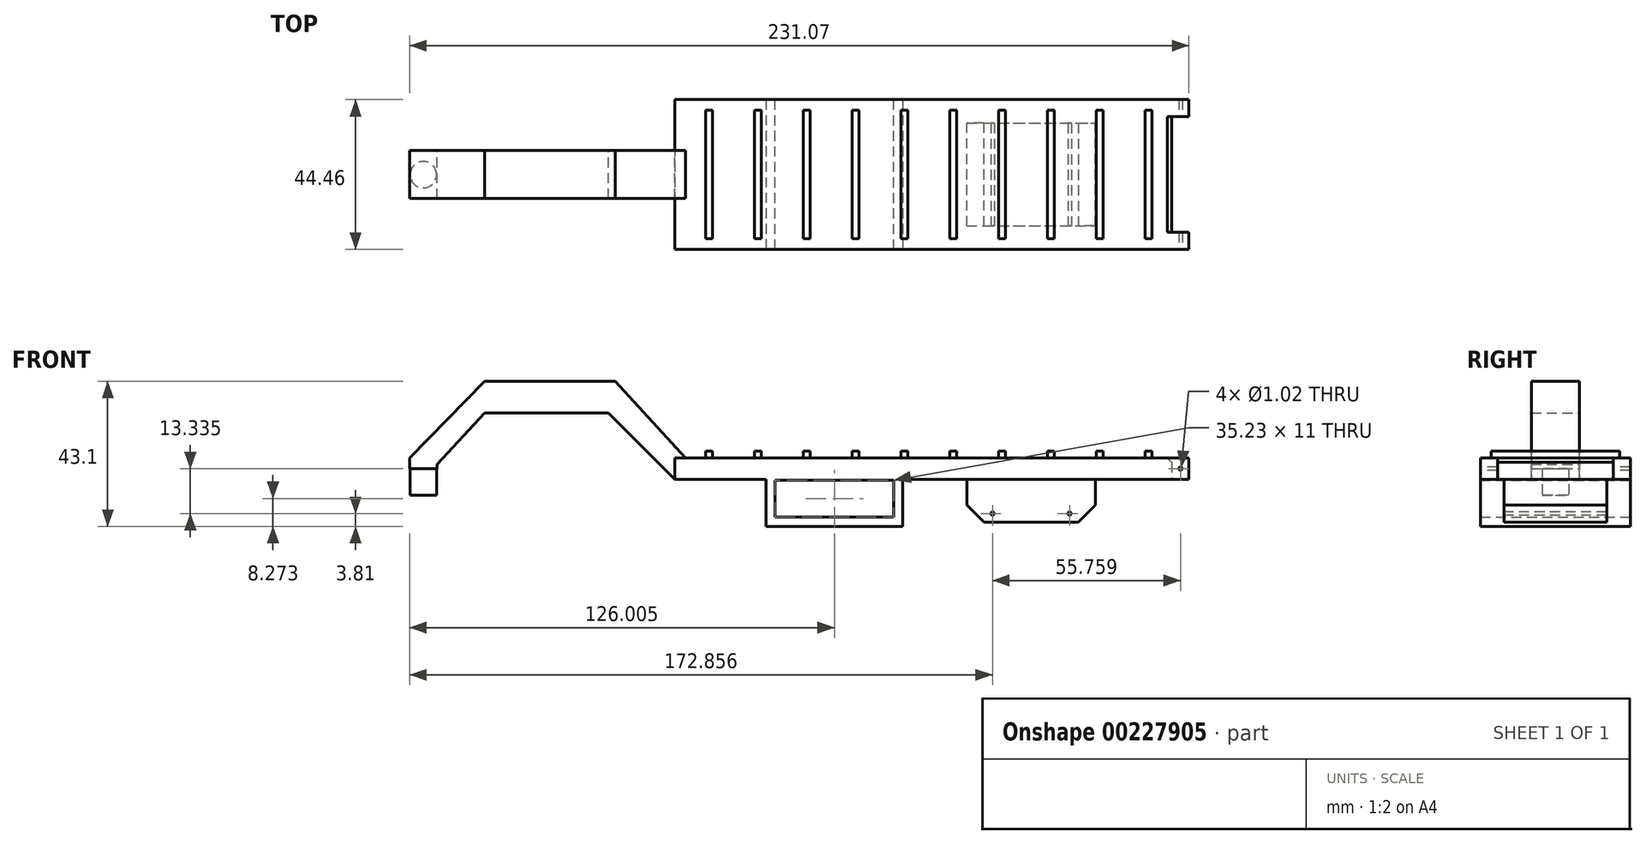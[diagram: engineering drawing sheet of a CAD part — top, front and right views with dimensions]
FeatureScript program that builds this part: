
annotation { "Feature Type Name" : "Feature", "Feature Type Description" : "" }
export const myFeature = defineFeature(function(context is Context, id is Id, definition is map)
    precondition{}
    {
        {
            var Q0;
            Q0=qCreatedBy(makeId("Top.planeOp"),FACE);
            var sketch = newSketch(context, id + "F0", { "sketchPlane" : qUnion([Q0])});
            skLineSegment(sketch, "E0.bottom", {"start": v(-76.2, 22.23) * mm, "end": v(76.2, 22.23) * mm});
            skLineSegment(sketch, "E0.top", {"start": v(-76.2, -22.23) * mm, "end": v(76.2, -22.23) * mm});
            skLineSegment(sketch, "E0.left", {"start": v(-76.2, 22.23) * mm, "end": v(-76.2, -22.23) * mm});
            skLineSegment(sketch, "E0.right", {"start": v(76.2, 22.23) * mm, "end": v(76.2, -22.23) * mm});
            skPoint(sketch, "E0.middle", {"position": v(0, 0) * mm});
            skSolve(sketch);
        }
        {
            var Q0;
            Q0=makeQuery(id+"F0.imprint","IMPRINT",FACE,{"disambiguationData":[TD([[makeQuery(id+"F0.imprint","IMPRINT",EDGE,{"derivedFrom":sQuery(id+"F0.wireOp",EDGE,"E0.bottom")}),-1.0]])]});
            extrude(context, id + "F1", {"entities" : qUnion([Q0]), "oppositeDirection" : true, "depth" : 6.35 * mm});
        }
        {
            var Q0;
            Q0=makeQuery(id+"F1.opExtrude","CAP_FACE",FACE,{"disambiguationData":[OSD([sQuery(id+"F0.wireOp",EDGE,"E0.bottom"),sQuery(id+"F0.wireOp",EDGE,"E0.top"),sQuery(id+"F0.wireOp",EDGE,"E0.left"),sQuery(id+"F0.wireOp",EDGE,"E0.right")])],"isStart":false});
            var sketch = newSketch(context, id + "F2", { "sketchPlane" : qUnion([Q0])});
            skLineSegment(sketch, "E1.bottom", {"start": v(10.37, 15.24) * mm, "end": v(48.47, 15.24) * mm});
            skLineSegment(sketch, "E1.top", {"start": v(10.37, -15.24) * mm, "end": v(48.47, -15.24) * mm});
            skLineSegment(sketch, "E1.left", {"start": v(10.37, 15.24) * mm, "end": v(10.37, -15.24) * mm});
            skLineSegment(sketch, "E1.right", {"start": v(48.47, 15.24) * mm, "end": v(48.47, -15.24) * mm});
            skPoint(sketch, "E1.middle", {"position": v(29.42, 0) * mm});
            skLineSegment(sketch, "E2.bottom", {"start": v(76.2, 17.14) * mm, "end": v(71.12, 17.14) * mm});
            skLineSegment(sketch, "E2.top", {"start": v(76.2, -17.14) * mm, "end": v(71.12, -17.14) * mm});
            skLineSegment(sketch, "E2.left", {"start": v(76.2, 17.14) * mm, "end": v(76.2, -17.14) * mm});
            skLineSegment(sketch, "E2.right", {"start": v(71.12, 17.14) * mm, "end": v(71.12, -17.14) * mm});
            skSolve(sketch);
        }
        {
            var Q0;
            Q0=makeQuery(id+"F2.imprint","IMPRINT",FACE,{"disambiguationData":[TD([[makeQuery(id+"F2.imprint","IMPRINT",EDGE,{"derivedFrom":sQuery(id+"F2.wireOp",EDGE,"E1.bottom")}),-1.0]])]});
            extrude(context, id + "F3", {"entities" : qUnion([Q0]), "operationType" : NewBodyOperationType.ADD, "depth" : 12.7 * mm});
        }
        {
            var Q0;
            Q0=makeQuery(id+"F2.imprint","IMPRINT",FACE,{"disambiguationData":[TD([[makeQuery(id+"F2.imprint","IMPRINT",EDGE,{"derivedFrom":sQuery(id+"F2.wireOp",EDGE,"E2.bottom")}),1.0]])]});
            extrude(context, id + "F4", {"entities" : qUnion([Q0]), "operationType" : NewBodyOperationType.REMOVE, "oppositeDirection" : true, "depth" : 25.4 * mm});
        }
        {
            var Q0;
            Q0=makeQuery(id+"F1.opExtrude","SWEPT_FACE",FACE,{"disambiguationData":[OSD([sQuery(id+"F0.wireOp",EDGE,"E0.top")])]});
            var sketch = newSketch(context, id + "F5", { "sketchPlane" : qUnion([Q0])});
            skCircle(sketch, "E3", {"center": v(73.74, -3.18) * mm, "radius": 0.5 * mm});
            skPoint(sketch, "E3.centerSnap0", {"position": v(76.2, -3.18) * mm});
            skSolve(sketch);
        }
        {
            var Q0;
            Q0=makeQuery(id+"F5.imprint","IMPRINT",FACE,{"disambiguationData":[TD([[makeQuery(id+"F5.imprint","IMPRINT",EDGE,{"derivedFrom":sQuery(id+"F5.wireOp",EDGE,"E3")}),1.0]])]});
            extrude(context, id + "F6", {"entities" : qUnion([Q0]), "operationType" : NewBodyOperationType.REMOVE, "oppositeDirection" : true, "depth" : 49.23 * mm});
        }
        {
            var Q0;
            Q0=makeQuery(id+"F3.opExtrude","CAP_EDGE",EDGE,{"disambiguationData":[OSD([sQuery(id+"F2.wireOp",EDGE,"E1.left")])],"isStart":false});
            var Q1;
            Q1=makeQuery(id+"F3.opExtrude","CAP_EDGE",EDGE,{"disambiguationData":[OSD([sQuery(id+"F2.wireOp",EDGE,"E1.right")])],"isStart":false});
            chamfer(context, id + "F7", {"entities" : qUnion([Q0, Q1]), "width" : 5.08 * mm, "tangentPropagation" : true});
        }
        {
            var Q0;
            Q0=makeQuery(id+"F4.boolean.opBoolean","INTERSECT",EDGE,{"derivedFrom":[makeQuery(id+"F1.opExtrude","CAP_FACE",FACE,{"disambiguationData":[OSD([sQuery(id+"F0.wireOp",EDGE,"E0.bottom"),sQuery(id+"F0.wireOp",EDGE,"E0.top"),sQuery(id+"F0.wireOp",EDGE,"E0.left"),sQuery(id+"F0.wireOp",EDGE,"E0.right")])],"isStart":true}),makeQuery(id+"F4.opExtrude","SWEPT_FACE",FACE,{"disambiguationData":[OSD([sQuery(id+"F2.wireOp",EDGE,"E2.right")])]})]});
            var Q1;
            Q1=makeQuery(id+"F4.boolean.opBoolean","COPY",EDGE,{"derivedFrom":makeQuery(id+"F4.opExtrude","CAP_EDGE",EDGE,{"disambiguationData":[OSD([sQuery(id+"F2.wireOp",EDGE,"E2.right")])],"isStart":true})});
            chamfer(context, id + "F8", {"entities" : qUnion([Q0, Q1]), "width" : 1.27 * mm, "tangentPropagation" : true});
        }
        {
            var Q0;
            Q0=qCreatedBy(makeId("Front.planeOp"),FACE);
            var sketch = newSketch(context, id + "F9", { "sketchPlane" : qUnion([Q0])});
            skLineSegment(sketch, "E4", {"start": v(-73, 0) * mm, "end": v(-93.79, 22.78) * mm});
            skLineSegment(sketch, "E5", {"start": v(-93.79, 22.78) * mm, "end": v(-132.6, 22.78) * mm});
            skLineSegment(sketch, "E6", {"start": v(-132.6, 22.78) * mm, "end": v(-154.87, 0) * mm});
            skLineSegment(sketch, "E7", {"start": v(-154.87, 0) * mm, "end": v(-154.87, -11.08) * mm});
            skLineSegment(sketch, "E8", {"start": v(-154.87, -11.08) * mm, "end": v(-146.63, -11.08) * mm});
            skLineSegment(sketch, "E9", {"start": v(-146.63, -11.08) * mm, "end": v(-146.63, -1.92) * mm});
            skLineSegment(sketch, "E10", {"start": v(-146.63, -1.92) * mm, "end": v(-132.6, 13.28) * mm});
            skLineSegment(sketch, "E11", {"start": v(-132.6, 13.28) * mm, "end": v(-95.88, 13.28) * mm});
            skLineSegment(sketch, "E12", {"start": v(-95.88, 13.28) * mm, "end": v(-76.2, -6.3) * mm});
            skLineSegment(sketch, "E13", {"start": v(-76.2, -6.3) * mm, "end": v(-76.2, 0) * mm});
            skLineSegment(sketch, "E14", {"start": v(-76.2, 0) * mm, "end": v(-73, 0) * mm});
            skSolve(sketch);
        }
        {
            var Q0;
            Q0=makeQuery(id+"F9.imprint","IMPRINT",FACE,{"disambiguationData":[TD([[makeQuery(id+"F9.imprint","IMPRINT",EDGE,{"derivedFrom":sQuery(id+"F9.wireOp",EDGE,"E4")}),1.0]])]});
            extrude(context, id + "F10", {"entities" : qUnion([Q0]), "operationType" : NewBodyOperationType.ADD, "endBound" : BoundingType.SYMMETRIC, "depth" : 14.22 * mm});
        }
        {
            var Q0;
            Q0=makeQuery(id+"F10.opExtrude","SWEPT_FACE",FACE,{"disambiguationData":[OSD([sQuery(id+"F9.wireOp",EDGE,"E8")])]});
            var sketch = newSketch(context, id + "F11", { "sketchPlane" : qUnion([Q0])});
            skCircle(sketch, "E15", {"center": v(-150.75, 0) * mm, "radius": 3.92 * mm});
            skPoint(sketch, "E15.centerSnap0", {"position": v(-150.75, 7.11) * mm});
            skLineSegment(sketch, "E16.bottom", {"start": v(-154.87, 7.11) * mm, "end": v(-146.63, 7.11) * mm});
            skLineSegment(sketch, "E16.top", {"start": v(-154.87, -7.11) * mm, "end": v(-146.63, -7.11) * mm});
            skLineSegment(sketch, "E16.left", {"start": v(-154.87, 7.11) * mm, "end": v(-154.87, -7.11) * mm});
            skLineSegment(sketch, "E16.right", {"start": v(-146.63, 7.11) * mm, "end": v(-146.63, -7.11) * mm});
            skSolve(sketch);
        }
        {
            var Q0;
            Q0=makeQuery(id+"F11.imprint","IMPRINT",FACE,{"disambiguationData":[TD([[makeQuery(id+"F11.imprint","IMPRINT",EDGE,{"derivedFrom":sQuery(id+"F11.wireOp",EDGE,"E15")}),-1.0]])]});
            extrude(context, id + "F12", {"entities" : qUnion([Q0]), "operationType" : NewBodyOperationType.REMOVE, "oppositeDirection" : true, "depth" : 7.87 * mm});
        }
        {
            var Q0;
            Q0=makeQuery(id+"F1.opExtrude","CAP_FACE",FACE,{"disambiguationData":[OSD([sQuery(id+"F0.wireOp",EDGE,"E0.bottom"),sQuery(id+"F0.wireOp",EDGE,"E0.top"),sQuery(id+"F0.wireOp",EDGE,"E0.left"),sQuery(id+"F0.wireOp",EDGE,"E0.right")])],"isStart":true});
            var sketch = newSketch(context, id + "F13", { "sketchPlane" : qUnion([Q0])});
            skLineSegment(sketch, "E17.bottom", {"start": v(-67, 19.05) * mm, "end": v(-64.96, 19.05) * mm});
            skLineSegment(sketch, "E17.top", {"start": v(-67, -19.05) * mm, "end": v(-64.96, -19.05) * mm});
            skLineSegment(sketch, "E17.left", {"start": v(-67, 19.05) * mm, "end": v(-67, -19.05) * mm});
            skLineSegment(sketch, "E17.right", {"start": v(-64.96, 19.05) * mm, "end": v(-64.96, -19.05) * mm});
            skPoint(sketch, "E17.middle", {"position": v(-65.98, 0) * mm});
            skLineSegment(sketch, "E18.1.0.0", {"start": v(-52.52, 19.05) * mm, "end": v(-50.48, 19.05) * mm});
            skLineSegment(sketch, "E18.1.0.1", {"start": v(-52.52, 19.05) * mm, "end": v(-52.52, -19.05) * mm});
            skLineSegment(sketch, "E18.1.0.2", {"start": v(-52.52, -19.05) * mm, "end": v(-50.48, -19.05) * mm});
            skLineSegment(sketch, "E18.1.0.3", {"start": v(-50.48, 19.05) * mm, "end": v(-50.48, -19.05) * mm});
            skLineSegment(sketch, "E18.2.0.0", {"start": v(-38.04, 19.05) * mm, "end": v(-36, 19.05) * mm});
            skLineSegment(sketch, "E18.2.0.1", {"start": v(-38.04, 19.05) * mm, "end": v(-38.04, -19.05) * mm});
            skLineSegment(sketch, "E18.2.0.2", {"start": v(-38.04, -19.05) * mm, "end": v(-36, -19.05) * mm});
            skLineSegment(sketch, "E18.2.0.3", {"start": v(-36, 19.05) * mm, "end": v(-36, -19.05) * mm});
            skLineSegment(sketch, "E18.3.0.0", {"start": v(-23.56, 19.05) * mm, "end": v(-21.53, 19.05) * mm});
            skLineSegment(sketch, "E18.3.0.1", {"start": v(-23.56, 19.05) * mm, "end": v(-23.56, -19.05) * mm});
            skLineSegment(sketch, "E18.3.0.2", {"start": v(-23.56, -19.05) * mm, "end": v(-21.53, -19.05) * mm});
            skLineSegment(sketch, "E18.3.0.3", {"start": v(-21.53, 19.05) * mm, "end": v(-21.53, -19.05) * mm});
            skLineSegment(sketch, "E18.4.0.0", {"start": v(-9.08, 19.05) * mm, "end": v(-7.05, 19.05) * mm});
            skLineSegment(sketch, "E18.4.0.1", {"start": v(-9.08, 19.05) * mm, "end": v(-9.08, -19.05) * mm});
            skLineSegment(sketch, "E18.4.0.2", {"start": v(-9.08, -19.05) * mm, "end": v(-7.05, -19.05) * mm});
            skLineSegment(sketch, "E18.4.0.3", {"start": v(-7.05, 19.05) * mm, "end": v(-7.05, -19.05) * mm});
            skLineSegment(sketch, "E18.5.0.0", {"start": v(5.4, 19.05) * mm, "end": v(7.43, 19.05) * mm});
            skLineSegment(sketch, "E18.5.0.1", {"start": v(5.4, 19.05) * mm, "end": v(5.4, -19.05) * mm});
            skLineSegment(sketch, "E18.5.0.2", {"start": v(5.4, -19.05) * mm, "end": v(7.43, -19.05) * mm});
            skLineSegment(sketch, "E18.5.0.3", {"start": v(7.43, 19.05) * mm, "end": v(7.43, -19.05) * mm});
            skLineSegment(sketch, "E18.6.0.0", {"start": v(19.87, 19.05) * mm, "end": v(21.9, 19.05) * mm});
            skLineSegment(sketch, "E18.6.0.1", {"start": v(19.87, 19.05) * mm, "end": v(19.87, -19.05) * mm});
            skLineSegment(sketch, "E18.6.0.2", {"start": v(19.87, -19.05) * mm, "end": v(21.9, -19.05) * mm});
            skLineSegment(sketch, "E18.6.0.3", {"start": v(21.9, 19.05) * mm, "end": v(21.9, -19.05) * mm});
            skLineSegment(sketch, "E18.7.0.0", {"start": v(34.35, 19.05) * mm, "end": v(36.38, 19.05) * mm});
            skLineSegment(sketch, "E18.7.0.1", {"start": v(34.35, 19.05) * mm, "end": v(34.35, -19.05) * mm});
            skLineSegment(sketch, "E18.7.0.2", {"start": v(34.35, -19.05) * mm, "end": v(36.38, -19.05) * mm});
            skLineSegment(sketch, "E18.7.0.3", {"start": v(36.38, 19.05) * mm, "end": v(36.38, -19.05) * mm});
            skLineSegment(sketch, "E18.8.0.0", {"start": v(48.83, 19.05) * mm, "end": v(50.86, 19.05) * mm});
            skLineSegment(sketch, "E18.8.0.1", {"start": v(48.83, 19.05) * mm, "end": v(48.83, -19.05) * mm});
            skLineSegment(sketch, "E18.8.0.2", {"start": v(48.83, -19.05) * mm, "end": v(50.86, -19.05) * mm});
            skLineSegment(sketch, "E18.8.0.3", {"start": v(50.86, 19.05) * mm, "end": v(50.86, -19.05) * mm});
            skLineSegment(sketch, "E18.9.0.0", {"start": v(63.3, 19.05) * mm, "end": v(65.34, 19.05) * mm});
            skLineSegment(sketch, "E18.9.0.1", {"start": v(63.3, 19.05) * mm, "end": v(63.3, -19.05) * mm});
            skLineSegment(sketch, "E18.9.0.2", {"start": v(63.3, -19.05) * mm, "end": v(65.34, -19.05) * mm});
            skLineSegment(sketch, "E18.9.0.3", {"start": v(65.34, 19.05) * mm, "end": v(65.34, -19.05) * mm});
            skLineSegment(sketch, "E18.direction1", {"start": v(-67, 19.05) * mm, "end": v(-52.52, 19.05) * mm, "construction": true});
            skSolve(sketch);
        }
        {
            var Q0;
            Q0=makeQuery(id+"F13.imprint","IMPRINT",FACE,{"disambiguationData":[TD([[makeQuery(id+"F13.imprint","IMPRINT",EDGE,{"derivedFrom":sQuery(id+"F13.wireOp",EDGE,"E17.bottom")}),-1.0]])]});
            var Q1;
            Q1=makeQuery(id+"F13.imprint","IMPRINT",FACE,{"disambiguationData":[TD([[makeQuery(id+"F13.imprint","IMPRINT",EDGE,{"derivedFrom":sQuery(id+"F13.wireOp",EDGE,"E18.1.0.0")}),-1.0]])]});
            var Q2;
            Q2=makeQuery(id+"F13.imprint","IMPRINT",FACE,{"disambiguationData":[TD([[makeQuery(id+"F13.imprint","IMPRINT",EDGE,{"derivedFrom":sQuery(id+"F13.wireOp",EDGE,"E18.2.0.0")}),-1.0]])]});
            var Q3;
            Q3=makeQuery(id+"F13.imprint","IMPRINT",FACE,{"disambiguationData":[TD([[makeQuery(id+"F13.imprint","IMPRINT",EDGE,{"derivedFrom":sQuery(id+"F13.wireOp",EDGE,"E18.3.0.0")}),-1.0]])]});
            var Q4;
            Q4=makeQuery(id+"F13.imprint","IMPRINT",FACE,{"disambiguationData":[TD([[makeQuery(id+"F13.imprint","IMPRINT",EDGE,{"derivedFrom":sQuery(id+"F13.wireOp",EDGE,"E18.4.0.0")}),-1.0]])]});
            var Q5;
            Q5=makeQuery(id+"F13.imprint","IMPRINT",FACE,{"disambiguationData":[TD([[makeQuery(id+"F13.imprint","IMPRINT",EDGE,{"derivedFrom":sQuery(id+"F13.wireOp",EDGE,"E18.5.0.0")}),-1.0]])]});
            var Q6;
            Q6=makeQuery(id+"F13.imprint","IMPRINT",FACE,{"disambiguationData":[TD([[makeQuery(id+"F13.imprint","IMPRINT",EDGE,{"derivedFrom":sQuery(id+"F13.wireOp",EDGE,"E18.6.0.0")}),-1.0]])]});
            var Q7;
            Q7=makeQuery(id+"F13.imprint","IMPRINT",FACE,{"disambiguationData":[TD([[makeQuery(id+"F13.imprint","IMPRINT",EDGE,{"derivedFrom":sQuery(id+"F13.wireOp",EDGE,"E18.7.0.0")}),-1.0]])]});
            var Q8;
            Q8=makeQuery(id+"F13.imprint","IMPRINT",FACE,{"disambiguationData":[TD([[makeQuery(id+"F13.imprint","IMPRINT",EDGE,{"derivedFrom":sQuery(id+"F13.wireOp",EDGE,"E18.8.0.0")}),-1.0]])]});
            var Q9;
            Q9=makeQuery(id+"F13.imprint","IMPRINT",FACE,{"disambiguationData":[TD([[makeQuery(id+"F13.imprint","IMPRINT",EDGE,{"derivedFrom":sQuery(id+"F13.wireOp",EDGE,"E18.9.0.0")}),-1.0]])]});
            extrude(context, id + "F14", {"entities" : qUnion([Q0, Q1, Q2, Q3, Q4, Q5, Q6, Q7, Q8, Q9]), "operationType" : NewBodyOperationType.ADD, "depth" : 2.03 * mm});
        }
        {
            var Q0;
            Q0=makeQuery(id+"F3.opExtrude","SWEPT_FACE",FACE,{"disambiguationData":[OSD([sQuery(id+"F2.wireOp",EDGE,"E1.bottom")])]});
            var sketch = newSketch(context, id + "F15", { "sketchPlane" : qUnion([Q0])});
            skLineSegment(sketch, "E19", {"start": v(7.7, -16.5) * mm, "end": v(12.9, -16.5) * mm, "construction": true});
            skPoint(sketch, "E19.startSnap0", {"position": v(12.9, -16.5) * mm});
            skCircle(sketch, "E20", {"center": v(17.99, -16.5) * mm, "radius": 0.5 * mm});
            skCircle(sketch, "E21", {"center": v(40.85, -16.5) * mm, "radius": 0.5 * mm});
            skLineSegment(sketch, "E22.trimOffspring", {"start": v(40.34, -16.5) * mm, "end": v(41.35, -16.5) * mm, "construction": true});
            skLineSegment(sketch, "E23.trimOffspring", {"start": v(17.48, -16.5) * mm, "end": v(18.5, -16.5) * mm, "construction": true});
            skSolve(sketch);
        }
        {
            var Q0;
            Q0=makeQuery(id+"F15.imprint","IMPRINT",FACE,{"disambiguationData":[TD([[makeQuery(id+"F15.imprint","IMPRINT",EDGE,{"derivedFrom":sQuery(id+"F15.wireOp",EDGE,"E20")}),1.0]])]});
            var Q1;
            Q1=makeQuery(id+"F15.imprint","IMPRINT",FACE,{"disambiguationData":[TD([[makeQuery(id+"F15.imprint","IMPRINT",EDGE,{"derivedFrom":sQuery(id+"F15.wireOp",EDGE,"E21")}),1.0]])]});
            extrude(context, id + "F16", {"entities" : qUnion([Q0, Q1]), "operationType" : NewBodyOperationType.REMOVE, "oppositeDirection" : true, "depth" : 33.27 * mm});
        }
        {
            var Q0;
            Q0=makeQuery(id+"F2.imprint","IMPRINT",FACE,{"disambiguationData":[TD([[makeQuery(id+"F2.imprint","IMPRINT",EDGE,{"derivedFrom":sQuery(id+"F2.wireOp",EDGE,"E1.bottom")}),1.0]])]});
            var sketch = newSketch(context, id + "F17", { "sketchPlane" : qUnion([Q0])});
            skLineSegment(sketch, "E24.bottom", {"start": v(-8.65, -22.23) * mm, "end": v(-49.1, -22.23) * mm});
            skLineSegment(sketch, "E24.top", {"start": v(-8.65, 22.23) * mm, "end": v(-49.1, 22.23) * mm});
            skLineSegment(sketch, "E24.left", {"start": v(-8.65, -22.23) * mm, "end": v(-8.65, 22.23) * mm});
            skLineSegment(sketch, "E24.right", {"start": v(-49.1, -22.23) * mm, "end": v(-49.1, 22.23) * mm});
            skPoint(sketch, "E24.middle", {"position": v(-28.88, 0) * mm});
            skSolve(sketch);
        }
        {
            var Q0;
            {var subQ0=sQuery(id+"F17.wireOp",EDGE,"E24.left");var subQ1=makeQuery(id+"F2.imprint","IMPRINT",EDGE,{"derivedFrom":makeQuery(id+"F1.opExtrude","CAP_EDGE",EDGE,{"disambiguationData":[OSD([sQuery(id+"F0.wireOp",EDGE,"E0.bottom")])],"isStart":false})});var subQ2=makeQuery(id+"F17.imprint","INTERSECT",VERTEX,{"derivedFrom":[subQ1,subQ0]});Q0=makeQuery(id+"F17.imprint","IMPRINT",FACE,{"disambiguationData":[TD([[makeQuery(id+"F17.imprint","IMPRINT",EDGE,{"disambiguationData":[TD([[subQ2,-1.0]])],"derivedFrom":subQ0}),1.0]])]});}
            extrude(context, id + "F18", {"entities" : qUnion([Q0]), "operationType" : NewBodyOperationType.ADD, "depth" : 13.97 * mm});
        }
        {
            var Q0;
            {var subQ0=sQuery(id+"F0.wireOp",EDGE,"E0.bottom");Q0=makeQuery(id+"F18.boolean.opBoolean","MERGE",FACE,{"derivedFrom":[makeQuery(id+"F1.opExtrude","SWEPT_FACE",FACE,{"disambiguationData":[OSD([subQ0])]}),makeQuery(id+"F18.opExtrude","SWEPT_FACE",FACE,{"disambiguationData":[OSD([subQ0])]})]});}
            var sketch = newSketch(context, id + "F19", { "sketchPlane" : qUnion([Q0])});
            skLineSegment(sketch, "E25.bottom", {"start": v(11.25, -17.55) * mm, "end": v(46.48, -17.55) * mm});
            skLineSegment(sketch, "E25.top", {"start": v(11.25, -6.55) * mm, "end": v(46.48, -6.55) * mm});
            skLineSegment(sketch, "E25.left", {"start": v(11.25, -17.55) * mm, "end": v(11.25, -6.55) * mm});
            skLineSegment(sketch, "E25.right", {"start": v(46.48, -17.55) * mm, "end": v(46.48, -6.55) * mm});
            skSolve(sketch);
        }
        {
            var Q0;
            Q0=makeQuery(id+"F19.imprint","IMPRINT",FACE,{"disambiguationData":[TD([[makeQuery(id+"F19.imprint","IMPRINT",EDGE,{"derivedFrom":sQuery(id+"F19.wireOp",EDGE,"E25.bottom")}),1.0]])]});
            extrude(context, id + "F20", {"entities" : qUnion([Q0]), "operationType" : NewBodyOperationType.REMOVE, "oppositeDirection" : true, "depth" : 53.1 * mm});
        }
        {
            var Q0;
            Q0=makeQuery(id+"F1.opExtrude","SWEPT_FACE",FACE,{"disambiguationData":[OSD([sQuery(id+"F0.wireOp",EDGE,"E0.left")])]});
            cPlane(context, id + "F21", {"entities" : qUnion([Q0]), "cplaneType" : CPlaneType.OFFSET, "offset" : 0 * mm, "width" : 152.4 * mm, "height" : 152.4 * mm});
        }
    });
